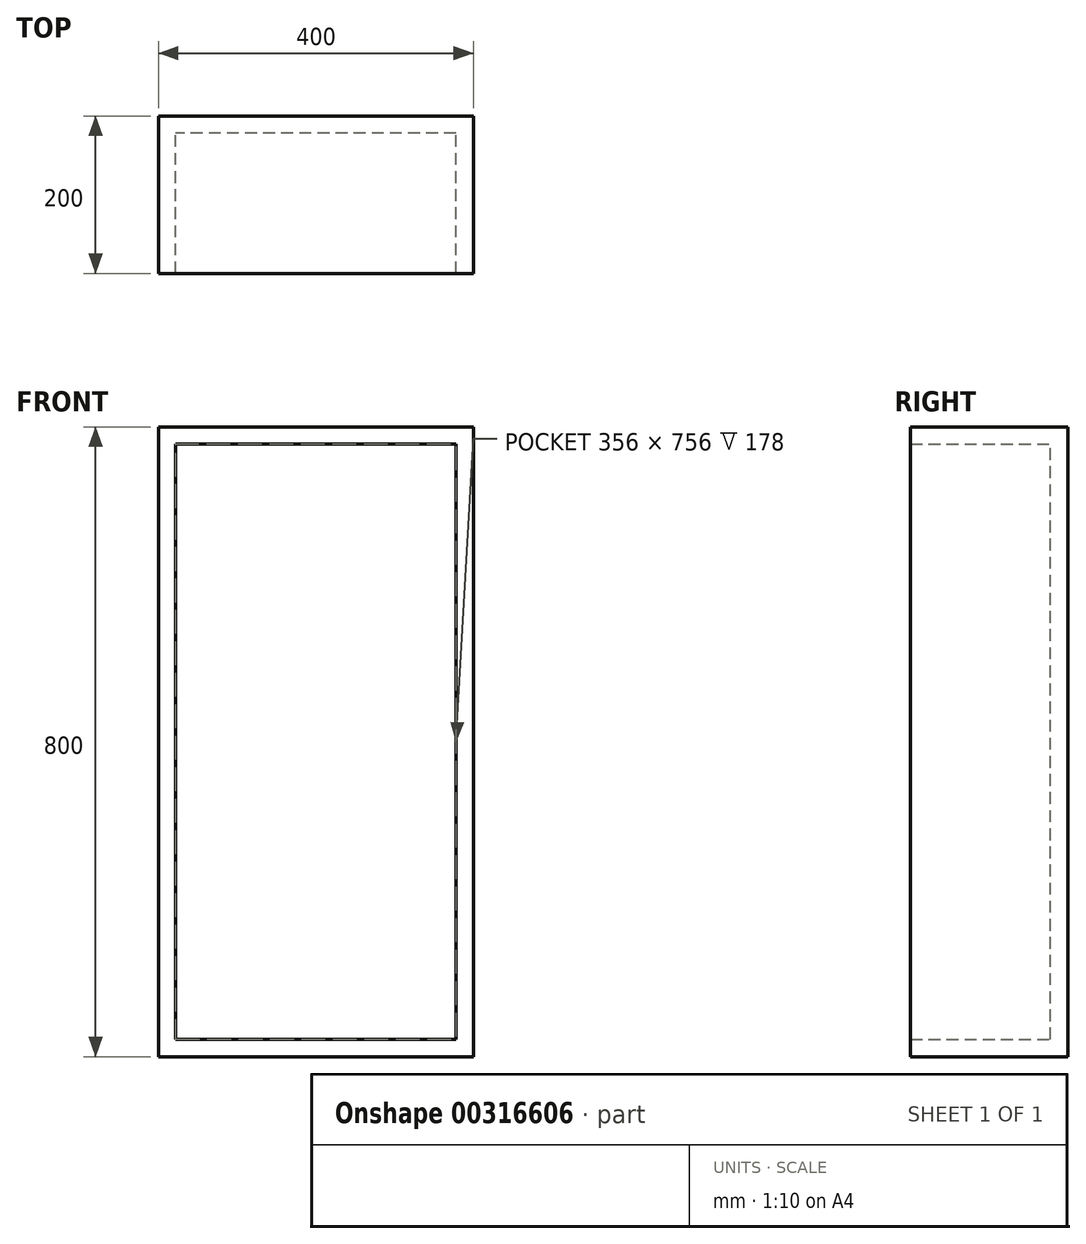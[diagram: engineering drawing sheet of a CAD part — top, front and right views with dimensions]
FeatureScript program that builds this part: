
annotation { "Feature Type Name" : "Feature", "Feature Type Description" : "" }
export const myFeature = defineFeature(function(context is Context, id is Id, definition is map)
    precondition{}
    {
        {
            var Q0;
            Q0=qCreatedBy(makeId("Front.planeOp"),FACE);
            var sketch = newSketch(context, id + "F0", { "sketchPlane" : qUnion([Q0])});
            skLineSegment(sketch, "E0.bottom", {"start": v(0, 0) * mm, "end": v(-400, 0) * mm});
            skLineSegment(sketch, "E0.top", {"start": v(0, 800) * mm, "end": v(-400, 800) * mm});
            skLineSegment(sketch, "E0.left", {"start": v(0, 0) * mm, "end": v(0, 800) * mm});
            skLineSegment(sketch, "E0.right", {"start": v(-400, 0) * mm, "end": v(-400, 800) * mm});
            skLineSegment(sketch, "E1.0", {"start": v(-378, 22) * mm, "end": v(-378, 778) * mm});
            skLineSegment(sketch, "E1.1", {"start": v(-22, 22) * mm, "end": v(-378, 22) * mm});
            skLineSegment(sketch, "E1.2", {"start": v(-22, 22) * mm, "end": v(-22, 778) * mm});
            skLineSegment(sketch, "E1.3", {"start": v(-22, 778) * mm, "end": v(-378, 778) * mm});
            skSolve(sketch);
        }
        {
            var Q0;
            Q0=makeQuery(id+"F0.imprint","IMPRINT",FACE,{"disambiguationData":[TD([[makeQuery(id+"F0.imprint","IMPRINT",EDGE,{"derivedFrom":sQuery(id+"F0.wireOp",EDGE,"E1.0")}),-1.0]])]});
            extrude(context, id + "F1", {"entities" : qUnion([Q0]), "depth" : 22 * mm});
        }
        {
            var Q0;
            Q0=makeQuery(id+"F0.imprint","IMPRINT",FACE,{"disambiguationData":[TD([[makeQuery(id+"F0.imprint","IMPRINT",EDGE,{"derivedFrom":sQuery(id+"F0.wireOp",EDGE,"E0.bottom")}),-1.0]])]});
            extrude(context, id + "F2", {"entities" : qUnion([Q0]), "operationType" : NewBodyOperationType.ADD, "depth" : 200 * mm});
        }
    });
